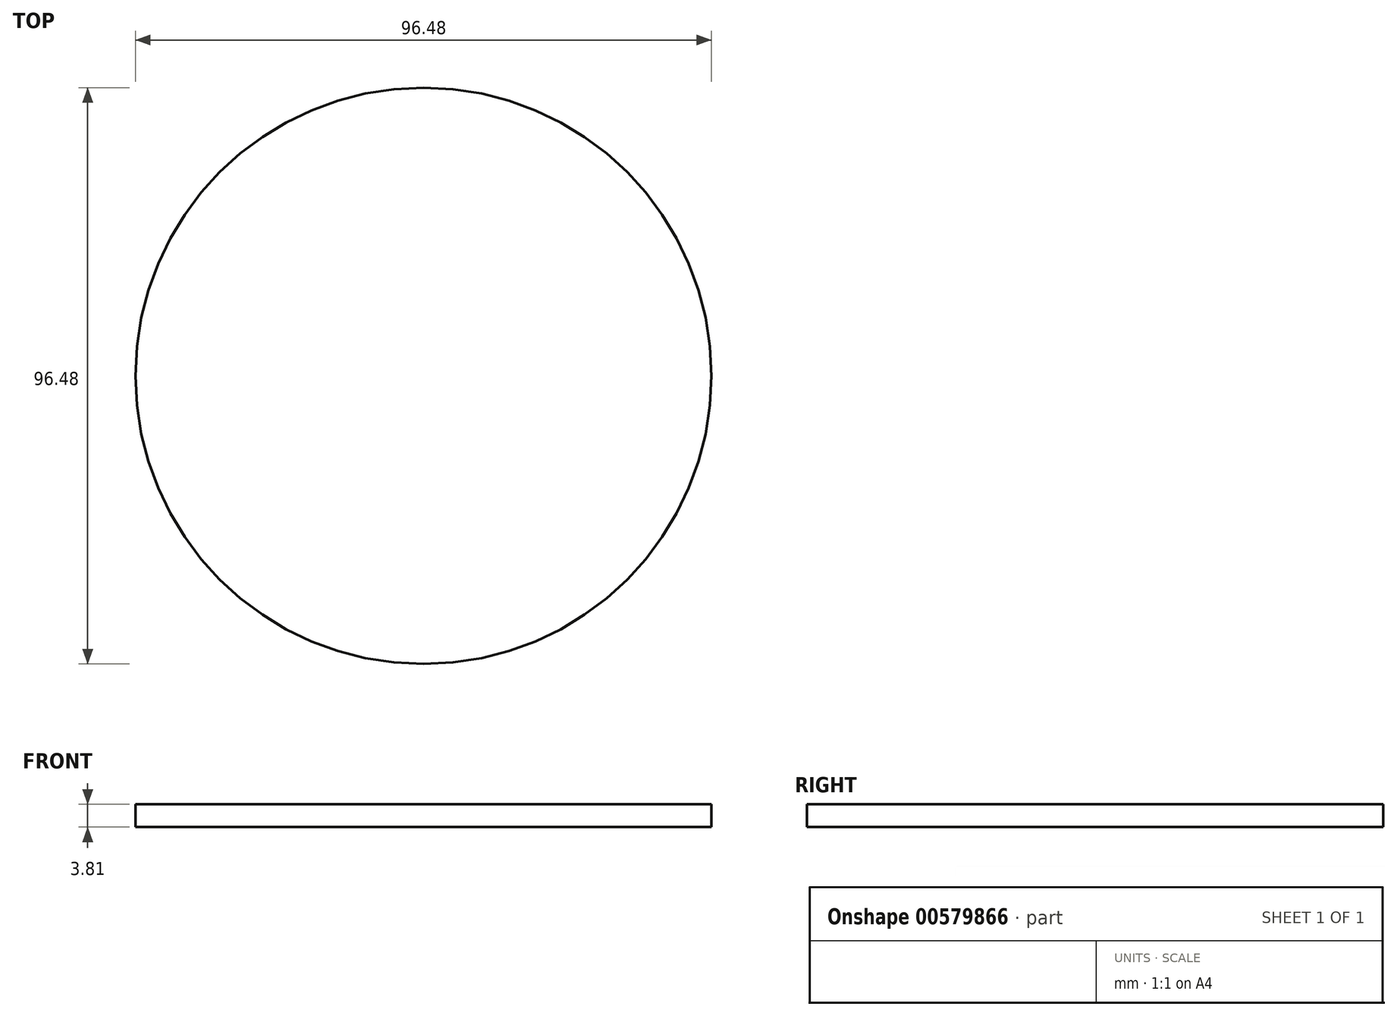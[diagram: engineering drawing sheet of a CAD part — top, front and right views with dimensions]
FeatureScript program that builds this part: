
annotation { "Feature Type Name" : "Feature", "Feature Type Description" : "" }
export const myFeature = defineFeature(function(context is Context, id is Id, definition is map)
    precondition{}
    {
        {
            var Q0;
            Q0=qCreatedBy(makeId("Top.planeOp"),FACE);
            var sketch = newSketch(context, id + "F0", { "sketchPlane" : qUnion([Q0])});
            skCircle(sketch, "E0", {"center": v(0, 0) * mm, "radius": 48.24 * mm});
            skSolve(sketch);
        }
        {
            var Q0;
            Q0 = qSketchRegion(id + "F0", true);
            extrude(context, id + "F1", {"entities" : qUnion([Q0]), "depth" : 3.8 * mm, "offsetDistance" : 25.4 * mm});
        }
    });
